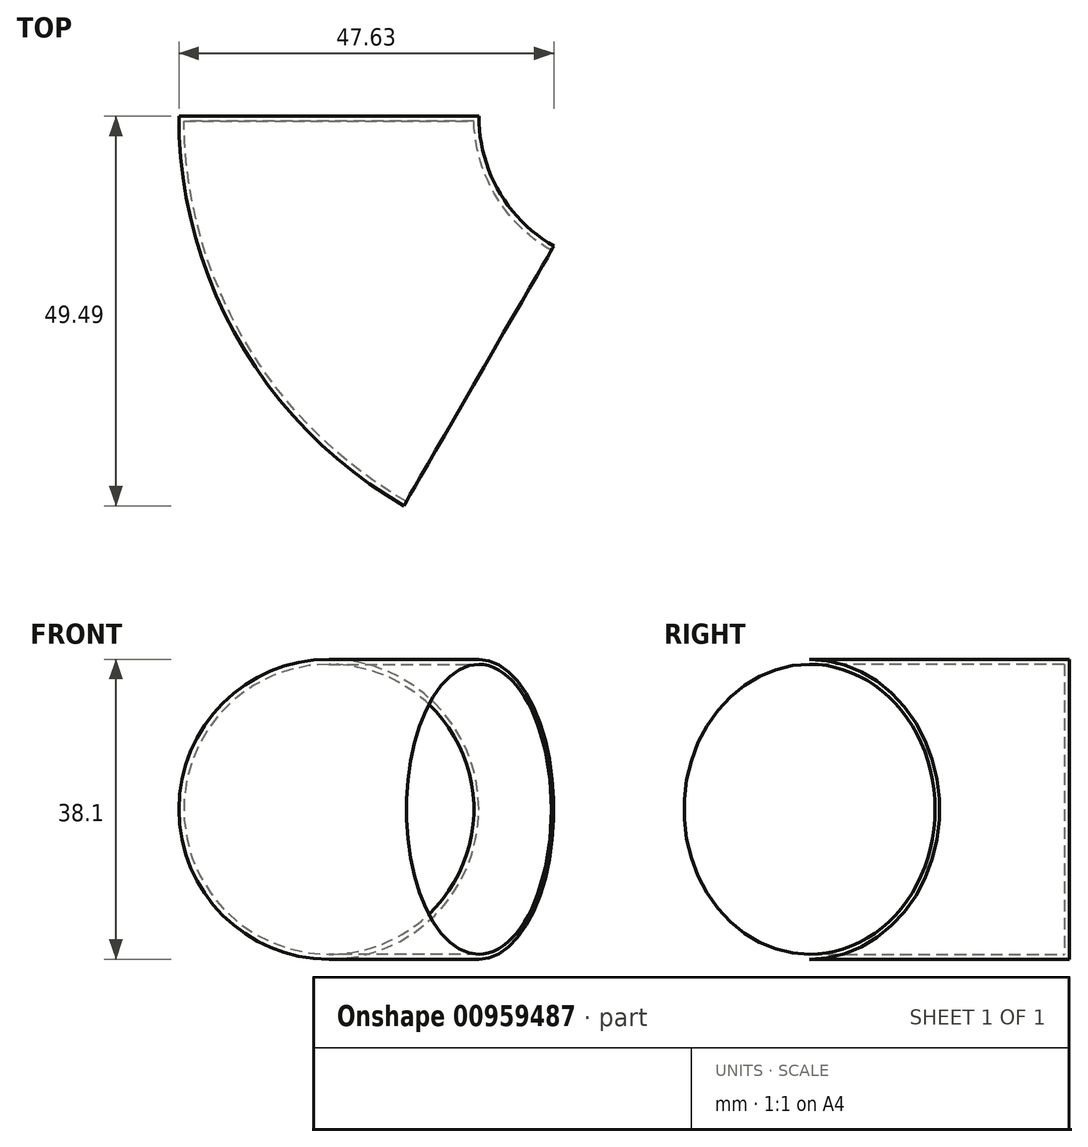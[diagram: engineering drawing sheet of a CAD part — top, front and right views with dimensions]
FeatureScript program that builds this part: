
annotation { "Feature Type Name" : "Feature", "Feature Type Description" : "" }
export const myFeature = defineFeature(function(context is Context, id is Id, definition is map)
    precondition{}
    {
        {
            var Q0;
            Q0=qCreatedBy(makeId("Front.planeOp"),FACE);
            var sketch = newSketch(context, id + "F0", { "sketchPlane" : qUnion([Q0])});
            skCircle(sketch, "E0", {"center": v(0, 0) * mm, "radius": 19.05 * mm});
            skSolve(sketch);
        }
        {
            var Q0;
            Q0=qCreatedBy(makeId("Top.planeOp"),FACE);
            var sketch = newSketch(context, id + "F1", { "sketchPlane" : qUnion([Q0])});
            skPoint(sketch, "E1", {"position": v(5.1, -19.05) * mm});
            skPoint(sketch, "E2", {"position": v(19.05, -33) * mm});
            skArc(sketch, "E3", {"start": v(0, 0) * mm, "mid": v(5.1, -19.05) * mm, "end": v(19.05, -33) * mm});
            skSolve(sketch);
        }
        {
            var Q0;
            Q0=makeQuery(id+"F0.imprint","IMPRINT",FACE,{"disambiguationData":[TD([[makeQuery(id+"F0.imprint","IMPRINT",EDGE,{"derivedFrom":sQuery(id+"F0.wireOp",EDGE,"E0")}),1.0]])]});
            var Q1;
            Q1=sQuery(id+"F1.wireOp",EDGE,"E3");
            sweep(context, id + "F2", {"profiles" : qUnion([Q0]), "path" : qUnion([Q1])});
        }
        {
            var Q0;
            Q0=makeQuery(id+"F2.opSweep","CAP_FACE",FACE,{"disambiguationData":[OSD([sQuery(id+"F0.wireOp",EDGE,"E0"),sQuery(id+"F1.wireOp",VERTEX,"E3.end")])],"isStart":false});
            shell(context, id + "F3", {"entities" : qUnion([Q0]), "thickness" : 0.64 * mm});
        }
    });
